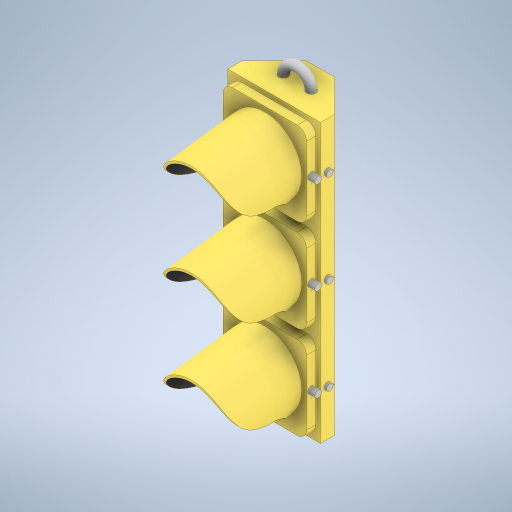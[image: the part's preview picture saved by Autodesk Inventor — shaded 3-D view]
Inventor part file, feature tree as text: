
AUTODESK INVENTOR PART (.ipt)
format: ipt  version: 2023.3 (Build 273359000, 359)  size: 484,864 bytes
history: mixed  units: in
note: dims shown in document units (in); Inventor stores cm internally (conversion verified against a paired STEP export)
features: sketch x6, sweep x6, extrude x1, plane x1, imported_body x1
ambient origin geometry x8: Origin, YZ Plane, XZ Plane, XY Plane, X Axis, Y Axis, Z Axis, Center Point
bodies: Solid2 (imported_parasolid), Solid1 (imported_parasolid)
feature tree (15):
  extrude  "Extrusion1"  Depth=0.08in
  plane  "Work Plane1"
  sketch  "Sketch3"  dims[d5=0.625in d6=0.0in d7=0.0in]
  sketch  "Sketch2"  dims[d2=0.08in d3=2.25in d4=0.0in]
  sweep  "Sweep1"
  sweep  "Sweep2"
  sweep  "Sweep3"
  sweep  "Sweep4"
  sweep  "Sweep5"
  sweep  "Sweep6"
  sketch  "Sketch1"  dims[d0=0.08in d1=0.08in]
  sketch  "Sketch4"  dims[d8=0.0in d9=0.0in d10=0.0in d11=0.0in]
  sketch  "Sketch5"  dims[d12=0.0in d13=0.0in d14=0.0in d15=0.0in]
  sketch  "Sketch6"  dims[d16=0.0in d17=0.0in]
  imported_body  NMx_Import_Brep_tag  [imported B-rep: ~14 faces, bbox_mm=[2.032035, 257.938707, 3.20057]]
